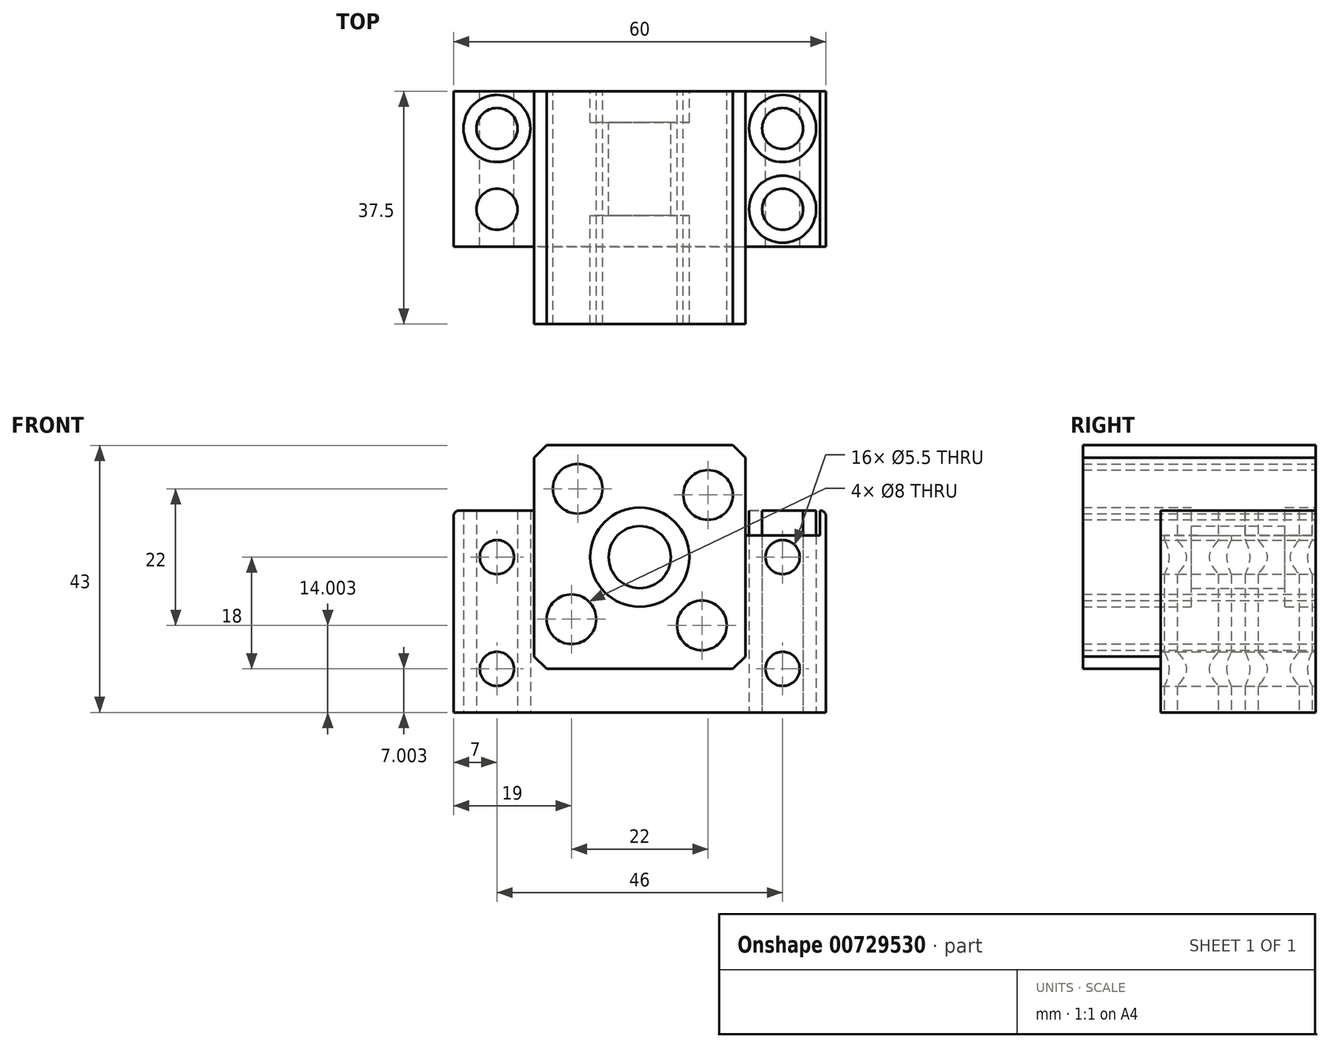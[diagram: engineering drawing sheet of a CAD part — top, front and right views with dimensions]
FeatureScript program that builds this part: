
annotation { "Feature Type Name" : "Feature", "Feature Type Description" : "" }
export const myFeature = defineFeature(function(context is Context, id is Id, definition is map)
    precondition{}
    {
        {
            var Q0;
            Q0=qCreatedBy(makeId("Front.planeOp"),FACE);
            var sketch = newSketch(context, id + "F0", { "sketchPlane" : qUnion([Q0])});
            skLineSegment(sketch, "E0", {"start": v(0, 62.09) * mm, "end": v(0, -50.94) * mm, "construction": true});
            skLineSegment(sketch, "E1.bottom", {"start": v(-30, 25.6) * mm, "end": v(-17, 25.6) * mm});
            skLineSegment(sketch, "E1.top", {"start": v(-30, -6.9) * mm, "end": v(30, -6.9) * mm});
            skLineSegment(sketch, "E1.left", {"start": v(-30, 25.6) * mm, "end": v(-30, -6.9) * mm});
            skLineSegment(sketch, "E1.right", {"start": v(30, 25.6) * mm, "end": v(30, -6.9) * mm});
            skLineSegment(sketch, "E2.top", {"start": v(-17, 36.1) * mm, "end": v(17, 36.1) * mm});
            skLineSegment(sketch, "E2.left", {"start": v(-17, 25.6) * mm, "end": v(-17, 36.1) * mm});
            skLineSegment(sketch, "E2.right", {"start": v(17, 25.6) * mm, "end": v(17, 36.1) * mm});
            skCircle(sketch, "E3", {"center": v(0, 18.1) * mm, "radius": 8 * mm});
            skCircle(sketch, "E4", {"center": v(0, 18.1) * mm, "radius": 5 * mm});
            skLineSegment(sketch, "E5", {"start": v(0, 18.1) * mm, "end": v(56.63, 18.1) * mm, "construction": true});
            skLineSegment(sketch, "E6", {"start": v(23, 31.07) * mm, "end": v(23, -27.42) * mm, "construction": true});
            skLineSegment(sketch, "E7.trimOffspring", {"start": v(17, 25.6) * mm, "end": v(30, 25.6) * mm});
            skLineSegment(sketch, "E8.MirrorCS", {"start": v(-23, 31.07) * mm, "end": v(-23, -27.42) * mm, "construction": true});
            skCircle(sketch, "E9", {"center": v(23, 18.1) * mm, "radius": 2.75 * mm});
            skCircle(sketch, "E10", {"center": v(23, 0.1) * mm, "radius": 2.75 * mm});
            skCircle(sketch, "E11.MirrorC", {"center": v(-23, 18.1) * mm, "radius": 2.75 * mm});
            skCircle(sketch, "E12.MirrorC", {"center": v(-23, 0.1) * mm, "radius": 2.75 * mm});
            skLineSegment(sketch, "E13.MirrorCS", {"start": v(-17, 0.1) * mm, "end": v(17, 0.1) * mm});
            skLineSegment(sketch, "E14", {"start": v(-17, 25.6) * mm, "end": v(-17, 0.1) * mm});
            skLineSegment(sketch, "E15", {"start": v(17, 25.6) * mm, "end": v(17, 0.1) * mm});
            skCircle(sketch, "E16", {"center": v(-10, 29.1) * mm, "radius": 4 * mm});
            skCircle(sketch, "E17.1.0", {"center": v(11, 28.1) * mm, "radius": 4 * mm});
            skCircle(sketch, "E17.2.0", {"center": v(10, 7.1) * mm, "radius": 4 * mm});
            skCircle(sketch, "E17.3.0", {"center": v(-11, 8.1) * mm, "radius": 4 * mm});
            skLineSegment(sketch, "E17.anchor1", {"start": v(0, 18.1) * mm, "end": v(-10, 29.1) * mm, "construction": true});
            skLineSegment(sketch, "E17.anchor2", {"start": v(0, 18.1) * mm, "end": v(-11, 8.1) * mm, "construction": true});
            skSolve(sketch);
        }
        {
            var Q0;
            Q0=qCreatedBy(makeId("Top.planeOp"),FACE);
            var sketch = newSketch(context, id + "F1", { "sketchPlane" : qUnion([Q0])});
            skLineSegment(sketch, "E18", {"start": v(23, 6.69) * mm, "end": v(23, 0) * mm, "construction": true});
            skCircle(sketch, "E19", {"center": v(23, 0) * mm, "radius": 3.3 * mm});
            skCircle(sketch, "E20", {"center": v(23, 0) * mm, "radius": 5.4 * mm});
            skLineSegment(sketch, "E21", {"start": v(0, 0) * mm, "end": v(0, 10.97) * mm, "construction": true});
            skLineSegment(sketch, "E22.MirrorCS", {"start": v(-23, 6.69) * mm, "end": v(-23, 0) * mm, "construction": true});
            skCircle(sketch, "E23.MirrorC", {"center": v(-23, 0) * mm, "radius": 5.4 * mm});
            skCircle(sketch, "E24.MirrorC", {"center": v(-23, 0) * mm, "radius": 3.3 * mm});
            skSolve(sketch);
        }
        {
            var Q0;
            Q0=makeQuery(id+"F0.imprint","IMPRINT",FACE,{"disambiguationData":[TD([[makeQuery(id+"F0.imprint","IMPRINT",EDGE,{"derivedFrom":sQuery(id+"F0.wireOp",EDGE,"E1.bottom")}),-1.0]])]});
            var Q1;
            Q1=makeQuery(id+"F0.imprint","IMPRINT",FACE,{"disambiguationData":[TD([[makeQuery(id+"F0.imprint","IMPRINT",EDGE,{"derivedFrom":sQuery(id+"F0.wireOp",EDGE,"E2.top")}),-1.0]])]});
            extrude(context, id + "F2", {"entities" : qUnion([Q0, Q1]), "depth" : 25 * mm, "offsetDistance" : 25 * mm, "symmetric" : true});
        }
        {
            var Q0;
            Q0=makeQuery(id+"F0.imprint","IMPRINT",FACE,{"disambiguationData":[TD([[makeQuery(id+"F0.imprint","IMPRINT",EDGE,{"derivedFrom":sQuery(id+"F0.wireOp",EDGE,"E3")}),1.0]])]});
            extrude(context, id + "F3", {"entities" : qUnion([Q0]), "operationType" : NewBodyOperationType.ADD, "depth" : 15 * mm, "offsetDistance" : 25 * mm, "symmetric" : true});
        }
        {
            var Q0;
            Q0=makeQuery(id+"F2.opExtrude","SWEPT_EDGE",EDGE,{"disambiguationData":[OSD([sQuery(id+"F0.wireOp",EDGE,"E1.bottom"),sQuery(id+"F0.wireOp",EDGE,"E1.left")])]});
            var Q1;
            Q1=makeQuery(id+"F2.opExtrude","SWEPT_EDGE",EDGE,{"disambiguationData":[OSD([sQuery(id+"F0.wireOp",EDGE,"E1.right"),sQuery(id+"F0.wireOp",EDGE,"E7.trimOffspring")])]});
            fillet(context, id + "F4", {"entities" : qUnion([Q0, Q1]), "radius" : 1 * mm, "tangentPropagation" : true, "allowEdgeOverflow" : false});
        }
        {
            var Q0;
            Q0=makeQuery(id+"F2.opExtrude","SWEPT_FACE",FACE,{"disambiguationData":[OSD([sQuery(id+"F0.wireOp",EDGE,"E1.top")])]});
            var sketch = newSketch(context, id + "F5", { "sketchPlane" : qUnion([Q0])});
            skLineSegment(sketch, "E25", {"start": v(23, 0.19) * mm, "end": v(23, -6.5) * mm, "construction": true});
            skCircle(sketch, "E26", {"center": v(23, -6.5) * mm, "radius": 3.3 * mm});
            skCircle(sketch, "E27", {"center": v(23, -6.5) * mm, "radius": 5.4 * mm});
            skLineSegment(sketch, "E28", {"start": v(0, -32.3) * mm, "end": v(0, 0) * mm, "construction": true});
            skLineSegment(sketch, "E29.MirrorCS", {"start": v(-23, 0.19) * mm, "end": v(-23, -6.5) * mm, "construction": true});
            skCircle(sketch, "E30.MirrorC", {"center": v(-23, -6.5) * mm, "radius": 5.4 * mm});
            skCircle(sketch, "E31.MirrorC", {"center": v(-23, -6.5) * mm, "radius": 3.3 * mm});
            skLineSegment(sketch, "E32", {"start": v(30, -12.5) * mm, "end": v(-30, -12.5) * mm});
            skLineSegment(sketch, "E33", {"start": v(-30, 0) * mm, "end": v(30, 0) * mm, "construction": true});
            skCircle(sketch, "E34.MirrorC", {"center": v(-23, 6.5) * mm, "radius": 5.4 * mm});
            skCircle(sketch, "E35.MirrorC", {"center": v(-23, 6.5) * mm, "radius": 3.3 * mm});
            skCircle(sketch, "E36.MirrorC", {"center": v(23, 6.5) * mm, "radius": 5.4 * mm});
            skCircle(sketch, "E37.MirrorC", {"center": v(23, 6.5) * mm, "radius": 3.3 * mm});
            skSolve(sketch);
        }
        {
            var Q0;
            Q0=makeQuery(id+"F5.imprint","IMPRINT",FACE,{"disambiguationData":[TD([[makeQuery(id+"F5.imprint","IMPRINT",EDGE,{"derivedFrom":sQuery(id+"F5.wireOp",EDGE,"E26")}),1.0]])]});
            var Q1;
            Q1=makeQuery(id+"F5.imprint","IMPRINT",FACE,{"disambiguationData":[TD([[makeQuery(id+"F5.imprint","IMPRINT",EDGE,{"derivedFrom":sQuery(id+"F5.wireOp",EDGE,"E31.MirrorC")}),-1.0]])]});
            var Q2;
            Q2=makeQuery(id+"F5.imprint","IMPRINT",FACE,{"disambiguationData":[TD([[makeQuery(id+"F5.imprint","IMPRINT",EDGE,{"derivedFrom":sQuery(id+"F5.wireOp",EDGE,"E35.MirrorC")}),1.0]])]});
            var Q3;
            Q3=makeQuery(id+"F5.imprint","IMPRINT",FACE,{"disambiguationData":[TD([[makeQuery(id+"F5.imprint","IMPRINT",EDGE,{"derivedFrom":sQuery(id+"F5.wireOp",EDGE,"E37.MirrorC")}),-1.0]])]});
            extrude(context, id + "F6", {"entities" : qUnion([Q0, Q1, Q2, Q3]), "operationType" : NewBodyOperationType.REMOVE, "oppositeDirection" : true, "depth" : 32.5 * mm, "offsetDistance" : 25 * mm});
        }
        {
            var Q0;
            Q0=makeQuery(id+"F2.opExtrude","SWEPT_FACE",FACE,{"disambiguationData":[OSD([sQuery(id+"F0.wireOp",EDGE,"E7.trimOffspring")])]});
            var sketch = newSketch(context, id + "F7", { "sketchPlane" : qUnion([Q0])});
            skLineSegment(sketch, "E38", {"start": v(23, 36.16) * mm, "end": v(23, -6.5) * mm, "construction": true});
            skCircle(sketch, "E39", {"center": v(23, -6.5) * mm, "radius": 3.3 * mm});
            skCircle(sketch, "E40", {"center": v(23, -6.5) * mm, "radius": 5.4 * mm});
            skLineSegment(sketch, "E41", {"start": v(0, 0) * mm, "end": v(0, 18.7) * mm, "construction": true});
            skLineSegment(sketch, "E42.MirrorCS", {"start": v(-23, 36.16) * mm, "end": v(-23, -6.5) * mm, "construction": true});
            skCircle(sketch, "E43.MirrorC", {"center": v(-23, -6.5) * mm, "radius": 5.4 * mm});
            skCircle(sketch, "E44.MirrorC", {"center": v(-23, -6.5) * mm, "radius": 3.3 * mm});
            skLineSegment(sketch, "E45", {"start": v(30, -12.5) * mm, "end": v(-30, -12.5) * mm});
            skLineSegment(sketch, "E46", {"start": v(-30, 0) * mm, "end": v(30, 0) * mm, "construction": true});
            skCircle(sketch, "E47.MirrorC", {"center": v(-23, 6.5) * mm, "radius": 5.4 * mm});
            skCircle(sketch, "E48.MirrorC", {"center": v(-23, 6.5) * mm, "radius": 3.3 * mm});
            skCircle(sketch, "E49.MirrorC", {"center": v(23, 6.5) * mm, "radius": 5.4 * mm});
            skCircle(sketch, "E50.MirrorC", {"center": v(23, 6.5) * mm, "radius": 3.3 * mm});
            skSolve(sketch);
        }
        {
            var Q0;
            Q0=makeQuery(id+"F0.imprint","IMPRINT",FACE,{"disambiguationData":[TD([[makeQuery(id+"F0.imprint","IMPRINT",EDGE,{"derivedFrom":sQuery(id+"F0.wireOp",EDGE,"E2.top")}),-1.0]])]});
            extrude(context, id + "F8", {"entities" : qUnion([Q0]), "operationType" : NewBodyOperationType.ADD, "depth" : 25 * mm, "offsetDistance" : 25 * mm});
        }
        {
            var Q0;
            {var subQ0=sQuery(id+"F0.wireOp",EDGE,"E2.left");var subQ1=sQuery(id+"F0.wireOp",EDGE,"E2.top");Q0=makeQuery(id+"F8.boolean.opBoolean","MERGE",EDGE,{"derivedFrom":[makeQuery(id+"F2.opExtrude","SWEPT_EDGE",EDGE,{"disambiguationData":[OSD([subQ1,subQ0])]}),makeQuery(id+"F8.opExtrude","SWEPT_EDGE",EDGE,{"disambiguationData":[OSD([subQ1,subQ0])]})]});}
            var Q1;
            {var subQ0=sQuery(id+"F0.wireOp",EDGE,"E2.right");var subQ1=sQuery(id+"F0.wireOp",EDGE,"E2.top");Q1=makeQuery(id+"F8.boolean.opBoolean","MERGE",EDGE,{"derivedFrom":[makeQuery(id+"F2.opExtrude","SWEPT_EDGE",EDGE,{"disambiguationData":[OSD([subQ1,subQ0])]}),makeQuery(id+"F8.opExtrude","SWEPT_EDGE",EDGE,{"disambiguationData":[OSD([subQ1,subQ0])]})]});}
            var Q2;
            Q2=makeQuery(id+"F8.opExtrude","SWEPT_EDGE",EDGE,{"disambiguationData":[OSD([sQuery(id+"F0.wireOp",EDGE,"E13.MirrorCS"),sQuery(id+"F0.wireOp",EDGE,"E15")])]});
            var Q3;
            Q3=makeQuery(id+"F8.opExtrude","SWEPT_EDGE",EDGE,{"disambiguationData":[OSD([sQuery(id+"F0.wireOp",EDGE,"E13.MirrorCS"),sQuery(id+"F0.wireOp",EDGE,"E14")])]});
            chamfer(context, id + "F9", {"entities" : qUnion([Q0, Q1, Q2, Q3]), "width" : 2 * mm, "tangentPropagation" : true});
        }
        {
            var Q0;
            Q0=makeQuery(id+"F7.imprint","IMPRINT",FACE,{"disambiguationData":[TD([[makeQuery(id+"F7.imprint","IMPRINT",EDGE,{"derivedFrom":sQuery(id+"F7.wireOp",EDGE,"E43.MirrorC")}),-1.0]])]});
            var Q1;
            Q1=makeQuery(id+"F7.imprint","IMPRINT",FACE,{"disambiguationData":[TD([[makeQuery(id+"F7.imprint","IMPRINT",EDGE,{"derivedFrom":sQuery(id+"F7.wireOp",EDGE,"E47.MirrorC")}),1.0]])]});
            var Q2;
            Q2=makeQuery(id+"F7.imprint","IMPRINT",FACE,{"disambiguationData":[TD([[makeQuery(id+"F7.imprint","IMPRINT",EDGE,{"derivedFrom":sQuery(id+"F7.wireOp",EDGE,"E39")}),-1.0]])]});
            var Q3;
            Q3=makeQuery(id+"F7.imprint","IMPRINT",FACE,{"disambiguationData":[TD([[makeQuery(id+"F7.imprint","IMPRINT",EDGE,{"derivedFrom":sQuery(id+"F7.wireOp",EDGE,"E49.MirrorC")}),-1.0]])]});
            extrude(context, id + "F10", {"entities" : qUnion([Q0, Q1, Q2, Q3]), "operationType" : NewBodyOperationType.REMOVE, "oppositeDirection" : true, "depth" : 4 * mm, "offsetDistance" : 25 * mm});
        }
    });
